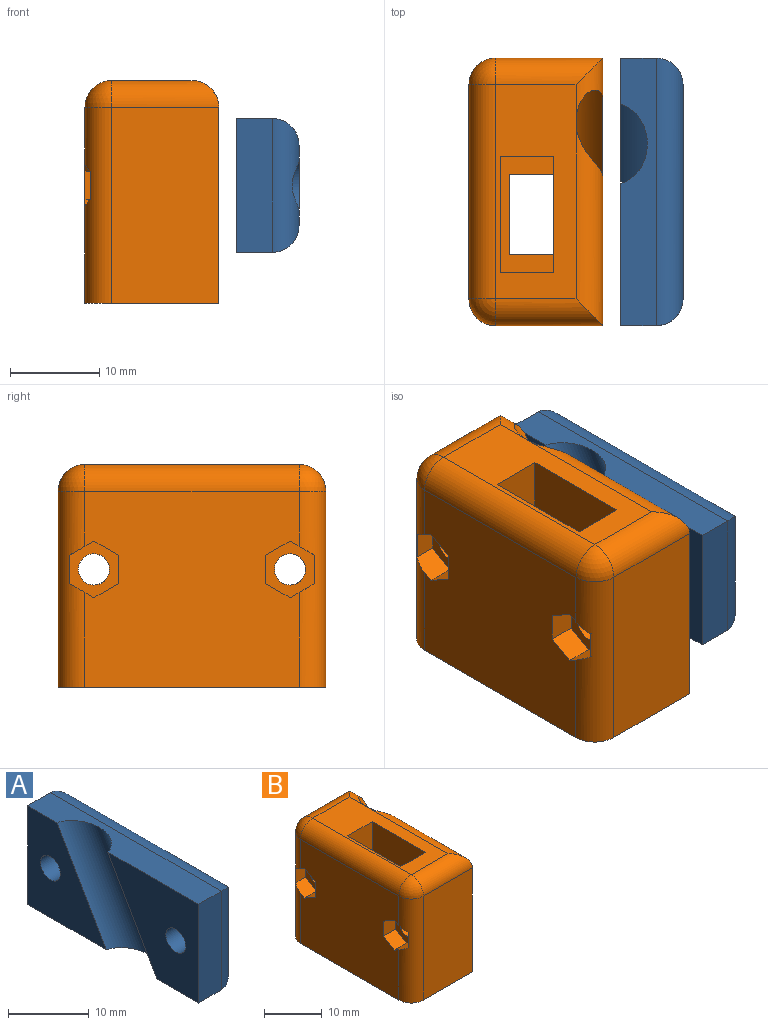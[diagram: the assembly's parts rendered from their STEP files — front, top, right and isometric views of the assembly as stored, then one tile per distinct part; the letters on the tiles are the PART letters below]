
ASSEMBLY  parts=2 mates=1
PART A: 18 faces, bbox 7x30x22.7 mm
  f0: plane 15.91x15mm, normal (-1,0,0), area 164.1mm2, adj f4,f5,f7,f12,f13
  f1: plane 15x13.8mm, normal (-1,0,0), area 132.5mm2, adj f2,f5,f6,f12,f13
  f2: plane 15x4mm, normal (0,1,0), area 60mm2, adj f1,f12,f13,f16
  f3: plane 24x9mm, normal (1,0,0), area 176mm2, adj f9,f11,f14,f15,f16,f17
  f4: plane 15x4mm, normal (0,-1,0), area 60mm2, adj f0,f12,f13,f15
  f5: cylinder r=4mm len=22.75mm, axis (0,-0.5,-0.87), area 182.6mm2, adj f0,f1,f12,f13
  f6: cylinder r=1.75mm len=4mm, axis (-1,0,0), area 44mm2, adj f1,f10
  f7: cylinder r=1.75mm len=4mm, axis (-1,0,0), area 44mm2, adj f0,f8
  f8: plane 6x6mm, normal (1,0,0), area 18.7mm2, adj f7,f9
  f9: cylinder r=3mm len=6mm, axis (1,0,0), area 53.8mm2, adj f3,f8,f15
  f10: plane 6x6mm, normal (1,0,0), area 18.7mm2, adj f6,f11
  f11: cylinder r=3mm len=6mm, axis (1,0,0), area 53.8mm2, adj f3,f10,f16
  f12: plane 30x4mm, normal (0,0,1), area 100.1mm2, adj f0,f1,f2,f4,f5,f14
  f13: plane 30x4mm, normal (0,0,-1), area 100.1mm2, adj f0,f1,f2,f4,f5,f17
  f14: cylinder r=3mm len=30mm, axis (0,1,0), area 131.1mm2, adj f3,f12,f15,f16
  f15: cylinder r=3mm len=15mm, axis (0,0,1), area 51.6mm2, adj f3,f4,f9,f14,f17
  f16: cylinder r=3mm len=15mm, axis (0,0,-1), area 51.6mm2, adj f2,f3,f11,f14,f17
  f17: cylinder r=3mm len=30mm, axis (0,-1,0), area 131.1mm2, adj f3,f13,f15,f16
PART B: 41 faces, bbox 15.1x30.1x32 mm
  f0: cylinder r=1.75mm len=12mm, axis (1,0,0), area 131.9mm2, adj f5,f25
  f1: cylinder r=1.75mm len=12mm, axis (1,0,0), area 131.9mm2, adj f2,f18
  f2: plane 22x16.64mm, normal (1,0,0), area 216.7mm2, adj f1,f3,f8,f17,f40
  f3: plane 30x15mm, normal (0,0,-1), area 381.3mm2, adj f2,f5,f6,f7,f8,f9,f14,f15
  f4: plane 24x9mm, normal (0,0,1), area 138mm2, adj f9,f10,f11,f12,f32,f34,f37,f39
  f5: plane 22x17.12mm, normal (1,0,0), area 227.2mm2, adj f0,f3,f6,f17,f32
  f6: plane 22x12mm, normal (0,1,0), area 264mm2, adj f3,f5,f33,f34
  f7: plane 24x22mm, normal (-1,0,0), area 490.3mm2, adj f3,f20,f21,f22,f23,f24,f26,f27
  f8: plane 22x12mm, normal (0,-1,0), area 264mm2, adj f2,f3,f36,f39
  f9: plane 25x13mm, normal (-1,0,0), area 281mm2, adj f3,f4,f10,f12,f13,f14,f16
  f10: plane 14x6mm, normal (0,-1,0), area 84mm2, adj f4,f9,f11,f13
  f11: plane 14x13mm, normal (1,0,0), area 182mm2, adj f4,f10,f12,f13
  f12: plane 14x6mm, normal (0,1,0), area 84mm2, adj f4,f9,f11,f13
  f13: plane 13x6mm, normal (0,0,1), area 33mm2, adj f9,f10,f11,f12,f14,f15,f16
  f14: plane 11x5mm, normal (0,-1,0), area 55mm2, adj f3,f9,f13,f15
  f15: plane 11x9mm, normal (1,0,0), area 99mm2, adj f3,f13,f14,f16
  f16: plane 11x5mm, normal (0,1,0), area 55mm2, adj f3,f9,f13,f15
  f17: cylinder r=4mm len=31.99mm, axis (0,-0.5,-0.87), area 299.3mm2, adj f2,f3,f5,f32,f40
  f18: plane 6.35x5.5mm, normal (-1,0,0), area 16.6mm2, adj f1,f19,f20,f21,f22,f23,f24
  f19: plane 3.18x2.44mm, normal (0,1,0), area 7.7mm2, adj f18,f20,f24,f36
  f20: plane 3.05x2.8mm, normal (0,0.5,-0.87), area 9.2mm2, adj f7,f18,f19,f21,f36
  f21: plane 3x2.75mm, normal (0,-0.5,-0.87), area 9.5mm2, adj f7,f18,f20,f22
  f22: plane 3.18x3mm, normal (0,-1,0), area 9.5mm2, adj f7,f18,f21,f23
  f23: plane 3x2.75mm, normal (0,-0.5,0.87), area 9.5mm2, adj f7,f18,f22,f24
  f24: plane 3.05x2.8mm, normal (0,0.5,0.87), area 9.2mm2, adj f7,f18,f19,f23,f36
  f25: plane 6.35x5.5mm, normal (-1,0,0), area 16.6mm2, adj f0,f26,f27,f28,f29,f30,f31
  f26: plane 3.18x3mm, normal (0,1,0), area 9.5mm2, adj f7,f25,f27,f31
  f27: plane 3x2.75mm, normal (0,0.5,-0.87), area 9.5mm2, adj f7,f25,f26,f28
  f28: plane 3.05x2.8mm, normal (0,-0.5,-0.87), area 9.2mm2, adj f7,f25,f27,f29,f33
  f29: plane 3.18x2.44mm, normal (0,-1,0), area 7.7mm2, adj f25,f28,f30,f33
  f30: plane 3.05x2.8mm, normal (0,-0.5,0.87), area 9.2mm2, adj f7,f25,f29,f31,f33
  f31: plane 3x2.75mm, normal (0,0.5,0.87), area 9.5mm2, adj f7,f25,f26,f30
  f32: cylinder r=3mm len=7.16mm, axis (0,-1,0), area 14.3mm2, adj f4,f5,f17,f34
  f33: cylinder r=3mm len=22mm, axis (0,0,-1), area 95.9mm2, adj f3,f6,f7,f28,f29,f30,f35
  f34: cylinder r=3mm len=12mm, axis (1,0,0), area 51.4mm2, adj f4,f6,f32,f35
  f35: sphere r=3mm, area 14.1mm2, adj f33,f34,f37
  f36: cylinder r=3mm len=22mm, axis (0,0,1), area 95.9mm2, adj f3,f7,f8,f19,f20,f24,f38
  f37: cylinder r=3mm len=24mm, axis (0,1,0), area 113.1mm2, adj f4,f7,f35,f38
  f38: sphere r=3mm, area 14.1mm2, adj f36,f37,f39
  f39: cylinder r=3mm len=12mm, axis (-1,0,0), area 51.4mm2, adj f4,f8,f38,f40
  f40: cylinder r=3mm len=22.84mm, axis (0,-1,0), area 82.3mm2, adj f2,f4,f17,f39
PLACE A t=(-7.17,-1.24,-2.95)mm
PLACE B t=(-13.17,-1.24,-2.95)mm
MATE fastened A.f6 <-> B.f0  axis (-1,0,0) through (-3.67,9.76,10.29)mm
